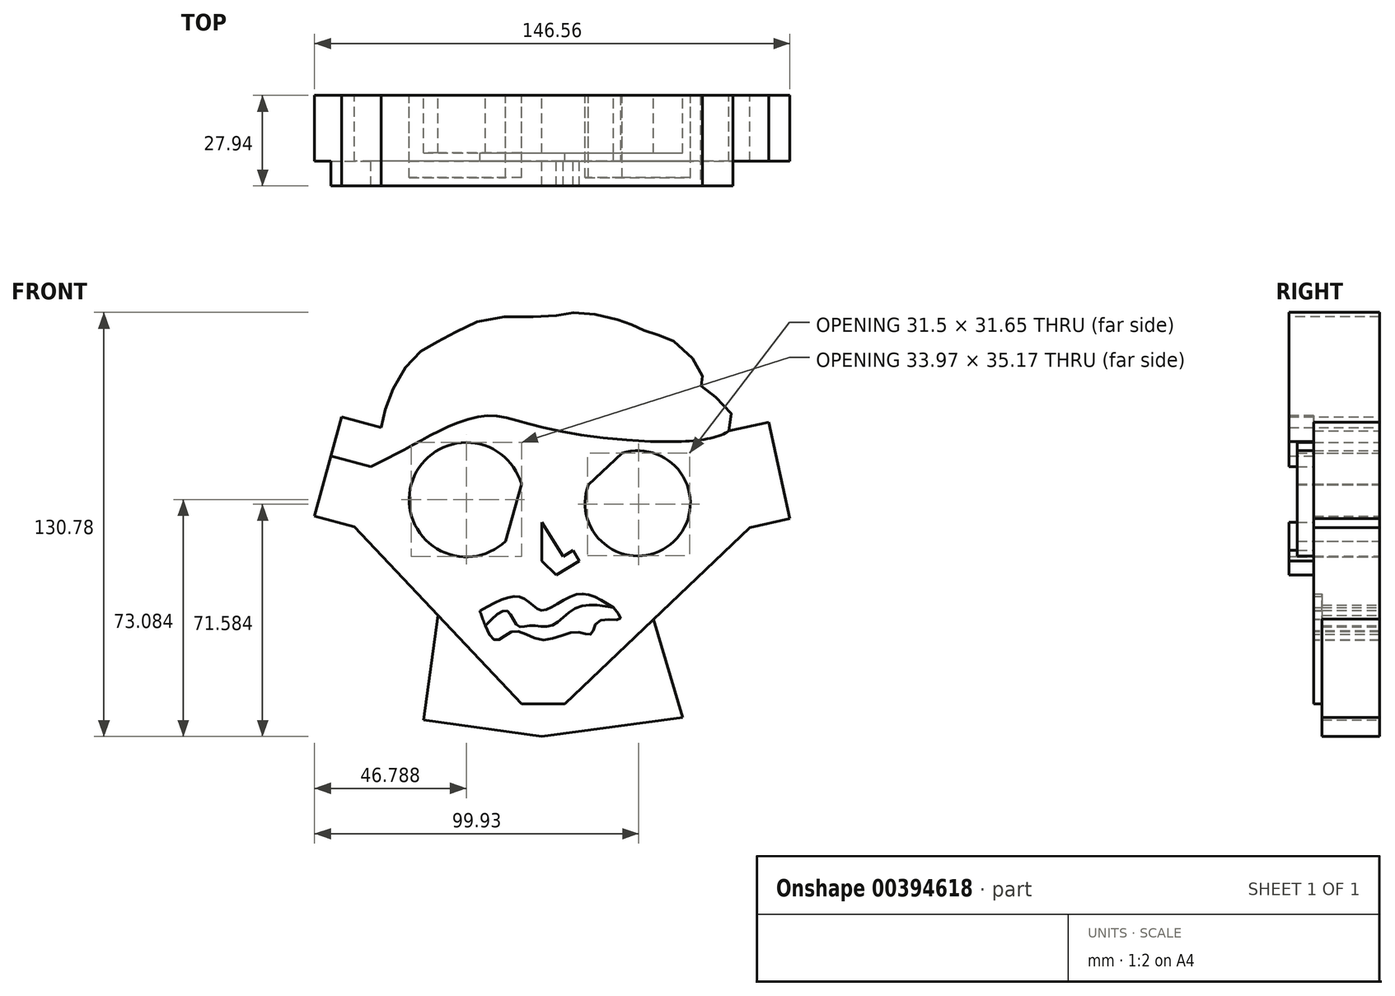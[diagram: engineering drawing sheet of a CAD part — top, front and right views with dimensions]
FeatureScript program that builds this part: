
annotation { "Feature Type Name" : "Feature", "Feature Type Description" : "" }
export const myFeature = defineFeature(function(context is Context, id is Id, definition is map)
    precondition{}
    {
        {
            var Q0;
            Q0=qCreatedBy(makeId("Front.planeOp"),FACE);
            var sketch = newSketch(context, id + "F0", { "sketchPlane" : qUnion([Q0])});
            skLineSegment(sketch, "E0", {"start": v(-6.29, -64.4) * mm, "end": v(7.1, -64.4) * mm});
            skLineSegment(sketch, "E1", {"start": v(7.1, -64.4) * mm, "end": v(64.09, -10.04) * mm});
            skLineSegment(sketch, "E2", {"start": v(64.09, -10.04) * mm, "end": v(57.6, 19.77) * mm});
            skLineSegment(sketch, "E3", {"start": v(-6.29, -64.4) * mm, "end": v(-57.8, -9.84) * mm});
            skLineSegment(sketch, "E4", {"start": v(-57.8, -9.84) * mm, "end": v(-49.49, 20.79) * mm});
            skFitSpline(sketch, "E5", {"points": [v(-19.06, -35.8) * mm, v(-6.29, -31.54) * mm, v(0, -35.6) * mm, v(10.55, -30.73) * mm, v(22.1, -34.78) * mm], "startDerivative": vector(51.82, 29.48) * mm, "endDerivative": vector(43.62, -28.5) * mm});
            skArc(sketch, "E6", {"start": v(-6.29, 3.35) * mm, "mid": v(-40.26, 3.22) * mm, "end": v(-11.15, -14.3) * mm});
            skArc(sketch, "E7", {"start": v(14.4, 3.18) * mm, "mid": v(40.69, -14.39) * mm, "end": v(24.74, 12.91) * mm});
            skLineSegment(sketch, "E8", {"start": v(0, -8.42) * mm, "end": v(0, -20.38) * mm});
            skLineSegment(sketch, "E9", {"start": v(0, -20.38) * mm, "end": v(4.46, -24.64) * mm});
            skLineSegment(sketch, "E10", {"start": v(4.46, -24.64) * mm, "end": v(11.56, -20.38) * mm});
            skLineSegment(sketch, "E11", {"start": v(11.56, -20.38) * mm, "end": v(9.6, -17.1) * mm});
            skLineSegment(sketch, "E12", {"start": v(9.6, -17.1) * mm, "end": v(6.55, -18.93) * mm});
            skFitSpline(sketch, "E13", {"points": [v(-49.49, 20.79) * mm, v(-46.85, 30.52) * mm, v(-38.74, 43.1) * mm, v(-30.22, 48.17) * mm, v(-16.83, 54.25) * mm, v(2.84, 55.06) * mm, v(11.36, 56.28) * mm, v(24.54, 53.64) * mm, v(28.8, 52.02) * mm, v(34.07, 49.8) * mm, v(40.36, 47.56) * mm, v(49.49, 37.01) * mm, v(48.88, 33.97) * mm, v(56.38, 27.89) * mm, v(57.6, 19.77) * mm, v(4.87, 19.77) * mm, v(-16.02, 24.44) * mm, v(-29.4, 20.79) * mm, v(-41.78, 14.3) * mm, v(-52.77, 8.7) * mm], "startDerivative": vector(37, 192.63) * mm, "endDerivative": vector(-206.56, -102.18) * mm});
            skLineSegment(sketch, "E14", {"start": v(-54.38, 2.78) * mm, "end": v(-61.25, 7.4) * mm});
            skLineSegment(sketch, "E15", {"start": v(-61.25, 7.4) * mm, "end": v(-67.74, -5.98) * mm});
            skLineSegment(sketch, "E16", {"start": v(-67.74, -5.98) * mm, "end": v(-62.26, -17.14) * mm});
            skLineSegment(sketch, "E17", {"start": v(-62.26, -17.14) * mm, "end": v(-53.38, -14.52) * mm});
            skLineSegment(sketch, "E18", {"start": v(60.84, 4.87) * mm, "end": v(65.91, 8.01) * mm});
            skLineSegment(sketch, "E19", {"start": v(65.91, 8.01) * mm, "end": v(72.66, -2.88) * mm});
            skLineSegment(sketch, "E20", {"start": v(72.66, -2.88) * mm, "end": v(70.38, -12.88) * mm});
            skLineSegment(sketch, "E21", {"start": v(70.38, -12.88) * mm, "end": v(61.48, -14.82) * mm});
            skLineSegment(sketch, "E22", {"start": v(-6.29, 3.35) * mm, "end": v(-11.15, -14.3) * mm});
            skLineSegment(sketch, "E23", {"start": v(24.74, 12.91) * mm, "end": v(14.4, 3.18) * mm});
            skLineSegment(sketch, "E24", {"start": v(10.75, 8.85) * mm, "end": v(20.28, 12.91) * mm});
            skLineSegment(sketch, "E25", {"start": v(20.28, 12.91) * mm, "end": v(33.48, 16.5) * mm});
            skLineSegment(sketch, "E26", {"start": v(-7.1, 15.1) * mm, "end": v(-25.55, 19.17) * mm});
            skLineSegment(sketch, "E27", {"start": v(34.42, -38.33) * mm, "end": v(43.4, -68.65) * mm});
            skLineSegment(sketch, "E28", {"start": v(-32.04, -37.11) * mm, "end": v(-36.5, -69.46) * mm});
            skLineSegment(sketch, "E29", {"start": v(-36.5, -69.46) * mm, "end": v(0, -74.5) * mm});
            skLineSegment(sketch, "E30", {"start": v(0, -74.5) * mm, "end": v(43.4, -68.65) * mm});
            skLineSegment(sketch, "E31", {"start": v(43.4, -68.65) * mm, "end": v(76.87, -75.55) * mm});
            skLineSegment(sketch, "E32", {"start": v(-36.5, -69.46) * mm, "end": v(-72.4, -76.36) * mm});
            skFitSpline(sketch, "E33", {"points": [v(-19.06, -35.8) * mm, v(-14.01, -44.9) * mm, v(-8.82, -42.06) * mm, v(0, -44.7) * mm, v(10.74, -42.23) * mm, v(15.2, -42.93) * mm, v(17.48, -38.98) * mm, v(24.06, -38.3) * mm, v(22.1, -34.78) * mm], "startDerivative": vector(30.06, -87.77) * mm, "endDerivative": vector(-40.3, 47.16) * mm});
            skFitSpline(sketch, "E34", {"points": [v(-17.51, -40.32) * mm, v(-10.7, -35.8) * mm, v(-7.49, -40.32) * mm, v(-3.3, -40.32) * mm, v(2.98, -40.32) * mm, v(10.74, -34.78) * mm, v(22.1, -34.78) * mm], "startDerivative": vector(44.32, 45.11) * mm, "endDerivative": vector(58.71, -10.86) * mm});
            skLineSegment(sketch, "E35", {"start": v(6.55, -18.93) * mm, "end": v(0, -8.42) * mm});
            skSolve(sketch);
        }
        {
            var Q0;
            Q0=makeQuery(id+"F0.imprint","IMPRINT",FACE,{"disambiguationData":[TD([[makeQuery(id+"F0.imprint","IMPRINT",EDGE,{"derivedFrom":sQuery(id+"F0.wireOp",EDGE,"E6")}),1.0]])]});
            extrude(context, id + "F1", {"entities" : qUnion([Q0]), "depth" : 25.4 * mm});
        }
        {
            var Q0;
            Q0=makeQuery(id+"F0.imprint","IMPRINT",FACE,{"disambiguationData":[TD([[makeQuery(id+"F0.imprint","IMPRINT",EDGE,{"derivedFrom":sQuery(id+"F0.wireOp",EDGE,"E7")}),1.0]])]});
            extrude(context, id + "F2", {"entities" : qUnion([Q0]), "depth" : 25.4 * mm});
        }
        {
            var Q0;
            {var subQ8=sQuery(id+"F0.wireOp",EDGE,"E0");Q0=makeQuery(id+"F0.imprint","IMPRINT",FACE,{"disambiguationData":[TD([[makeQuery(id+"F0.imprint","IMPRINT",EDGE,{"derivedFrom":subQ8}),1.0]])]});}
            extrude(context, id + "F3", {"entities" : qUnion([Q0]), "depth" : 20.32 * mm});
        }
        {
            var Q0;
            {var subQ0=sQuery(id+"F0.wireOp",EDGE,"E13");var subQ4=makeQuery(id+"F0.imprint","IMPRINT",VERTEX,{"derivedFrom":subQ0});Q0=makeQuery(id+"F0.imprint","IMPRINT",FACE,{"disambiguationData":[TD([[makeQuery(id+"F0.imprint","IMPRINT",EDGE,{"disambiguationData":[TD([[subQ4,1.0]])],"derivedFrom":subQ0}),-1.0]])]});}
            extrude(context, id + "F4", {"entities" : qUnion([Q0]), "operationType" : NewBodyOperationType.ADD, "depth" : 27.94 * mm});
        }
        {
            var Q0;
            Q0=makeQuery(id+"F3.opExtrude","SWEPT_FACE",FACE,{"disambiguationData":[OSD([sQuery(id+"F0.wireOp",EDGE,"E2")])]});
            extrude(context, id + "F5", {"entities" : qUnion([Q0]), "operationType" : NewBodyOperationType.ADD, "depth" : 12.7 * mm});
        }
        {
            var Q0;
            {var subQ0=sQuery(id+"F0.wireOp",EDGE,"E4");Q0=makeQuery(id+"F4.boolean.opBoolean","MERGE",FACE,{"derivedFrom":[makeQuery(id+"F3.opExtrude","SWEPT_FACE",FACE,{"disambiguationData":[OSD([subQ0])]}),makeQuery(id+"F4.opExtrude","SWEPT_FACE",FACE,{"disambiguationData":[OSD([subQ0])]})]});}
            extrude(context, id + "F6", {"entities" : qUnion([Q0]), "operationType" : NewBodyOperationType.ADD, "depth" : 12.7 * mm});
        }
        {
            var Q0;
            {var subQ2=sQuery(id+"F0.wireOp",EDGE,"E0");Q0=makeQuery(id+"F0.imprint","IMPRINT",FACE,{"disambiguationData":[TD([[makeQuery(id+"F0.imprint","IMPRINT",EDGE,{"derivedFrom":subQ2}),-1.0]])]});}
            extrude(context, id + "F7", {"entities" : qUnion([Q0]), "operationType" : NewBodyOperationType.ADD, "depth" : 17.78 * mm});
        }
        {
            var Q0;
            {var subQ0=sQuery(id+"F0.wireOp",EDGE,"E5");Q0=makeQuery(id+"F0.imprint","IMPRINT",FACE,{"disambiguationData":[TD([[makeQuery(id+"F0.imprint","IMPRINT",EDGE,{"derivedFrom":subQ0}),-1.0]])]});}
            extrude(context, id + "F8", {"entities" : qUnion([Q0]), "operationType" : NewBodyOperationType.ADD, "depth" : 17.78 * mm});
        }
        {
            var Q0;
            Q0=makeQuery(id+"F0.imprint","IMPRINT",FACE,{"disambiguationData":[TD([[makeQuery(id+"F0.imprint","IMPRINT",EDGE,{"derivedFrom":sQuery(id+"F0.wireOp",EDGE,"E8")}),1.0]])]});
            extrude(context, id + "F9", {"entities" : qUnion([Q0]), "operationType" : NewBodyOperationType.ADD, "depth" : 27.94 * mm});
        }
    });
